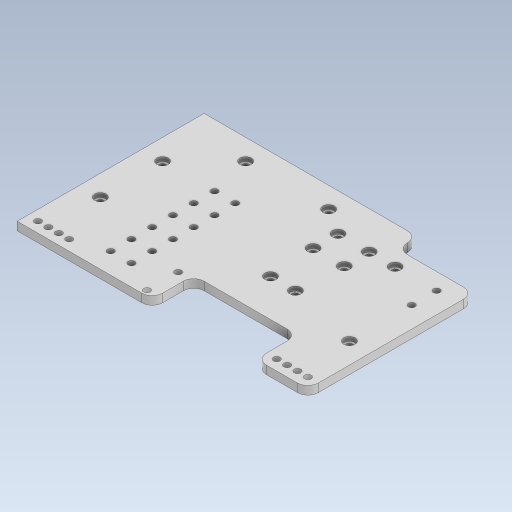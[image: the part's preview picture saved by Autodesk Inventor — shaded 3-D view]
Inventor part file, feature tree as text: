
AUTODESK INVENTOR PART (.ipt)
format: ipt  version: 2023.5 (Build 275446000, 446)  size: 252,928 bytes
history: native  units: mm
features: extrude x2, sketch x1, fillet x1
ambient origin geometry x8: Origin, YZ Plane, XZ Plane, XY Plane, X Axis, Y Axis, Z Axis, Center Point
bodies: Solid1 (feature_tree)
feature tree (4):
  sketch  "Sketch1"  dims[d29=90.0mm d30=140.0mm d31=3.2mm d32=30.0mm d33=10.0mm d34=5.5mm d35=3.2mm d36=5.5mm d37=4.0mm d38=0.0mm d39=2.0mm d40=0.0mm d41=10.0mm d42=10.0mm d43=10.0mm d44=10.0mm d45=10.0mm d46=3.2mm d47=5.0mm d48=2.5mm d49=3.2mm d50=15.0mm d51=3.2mm d53=20.0mm d61=3.2mm d62=10.0mm d63=3.2mm d64=10.0mm d65=3.2mm d66=10.0mm d67=10.0mm d68=3.2mm d69=10.0mm d70=3.2mm d71=10.0mm d72=3.2mm d73=3.2mm d74=3.2mm d75=10.0mm d76=3.2mm d77=10.0mm d78=3.2mm d79=3.2mm d80=3.3mm d81=5.0mm d82=5.0mm d83=3.2mm d84=5.5mm d85=3.2mm d86=3.2mm d87=10.0mm]
  extrude  "Extrusion1"  Depth=140.0mm
  extrude  "Extrusion2"  Depth=10.0mm
  fillet  "Fillet1"  Radius=30.0mm
